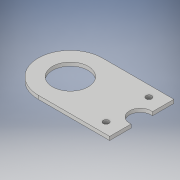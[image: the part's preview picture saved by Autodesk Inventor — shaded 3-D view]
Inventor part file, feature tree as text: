
AUTODESK INVENTOR PART (.ipt)
format: ipt  version: 2019 (Build 230136000, 136)  size: 119,808 bytes
history: native  units: in
note: dims shown in document units (in); Inventor stores cm internally (conversion verified against a paired STEP export)
features: extrude x1, sketch x1
ambient origin geometry x8: Origin, YZ Plane, XZ Plane, XY Plane, X Axis, Y Axis, Z Axis, Center Point
bodies: Solid1 (feature_tree)
feature tree (2):
  extrude  "Extrusion1"  Depth=0.125in
  sketch  "Sketch1"  dims[d0=1.25in d1=0.5in d2=2.5in d3=0.75in d4=0.75in d5=0.5in d6=2.5in d7=0.75in d8=0.75in d9=0.2031in d10=0.2031in d11=0.125in d12=0.0in]
